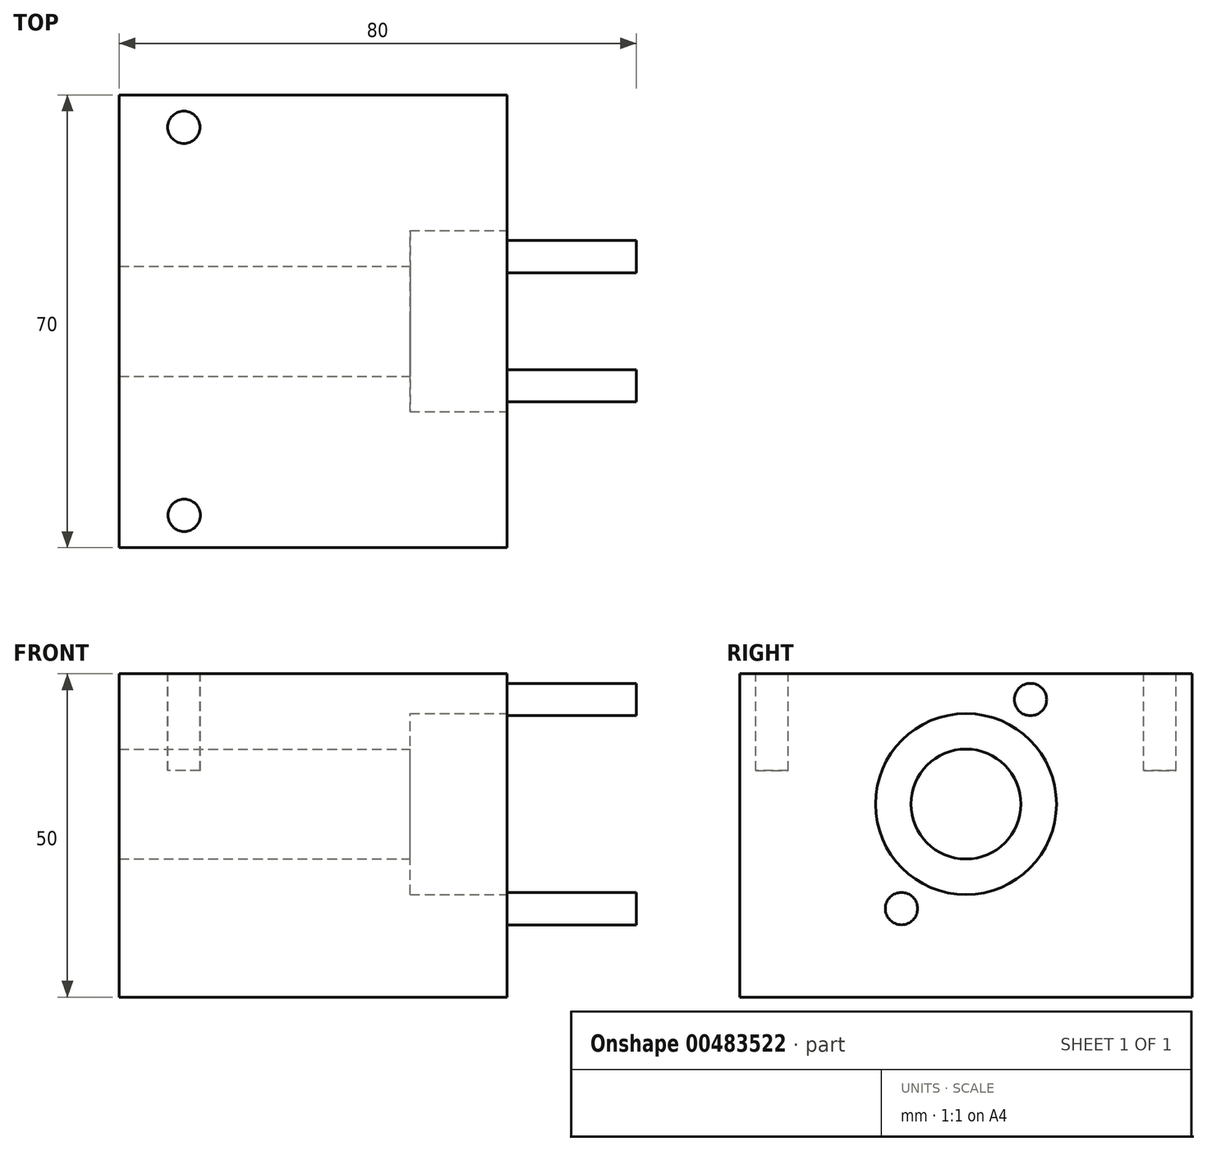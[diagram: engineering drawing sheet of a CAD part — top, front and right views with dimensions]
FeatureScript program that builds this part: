
annotation { "Feature Type Name" : "Feature", "Feature Type Description" : "" }
export const myFeature = defineFeature(function(context is Context, id is Id, definition is map)
    precondition{}
    {
        {
            var Q0;
            Q0=qCreatedBy(makeId("Top.planeOp"),FACE);
            var sketch = newSketch(context, id + "F0", { "sketchPlane" : qUnion([Q0])});
            skLineSegment(sketch, "E0.bottom", {"start": v(-38.54, 38.67) * mm, "end": v(41.46, 38.67) * mm});
            skLineSegment(sketch, "E0.top", {"start": v(-38.54, -31.33) * mm, "end": v(41.46, -31.33) * mm});
            skLineSegment(sketch, "E0.left", {"start": v(-38.54, 38.67) * mm, "end": v(-38.54, -31.33) * mm});
            skLineSegment(sketch, "E0.right", {"start": v(41.46, 38.67) * mm, "end": v(41.46, -31.33) * mm});
            skSolve(sketch);
        }
        {
            var Q0;
            Q0=makeQuery(id+"F0.imprint","IMPRINT",FACE,{"disambiguationData":[TD([[makeQuery(id+"F0.imprint","IMPRINT",EDGE,{"derivedFrom":sQuery(id+"F0.wireOp",EDGE,"E0.bottom")}),-1.0]])]});
            extrude(context, id + "F1", {"entities" : qUnion([Q0]), "depth" : 50 * mm});
        }
        {
            var Q0;
            Q0=makeQuery(id+"F1.opExtrude","CAP_FACE",FACE,{"disambiguationData":[OSD([sQuery(id+"F0.wireOp",EDGE,"E0.bottom"),sQuery(id+"F0.wireOp",EDGE,"E0.top"),sQuery(id+"F0.wireOp",EDGE,"E0.left"),sQuery(id+"F0.wireOp",EDGE,"E0.right")])],"isStart":false});
            var sketch = newSketch(context, id + "F2", { "sketchPlane" : qUnion([Q0])});
            skCircle(sketch, "E1", {"center": v(-28.54, 33.67) * mm, "radius": 2.5 * mm});
            skCircle(sketch, "E2.0.1.0", {"center": v(-28.48, -26.33) * mm, "radius": 2.5 * mm});
            skCircle(sketch, "E2.1.0.0", {"center": v(31.46, 33.52) * mm, "radius": 2.5 * mm});
            skCircle(sketch, "E2.1.1.0", {"center": v(31.52, -26.48) * mm, "radius": 2.5 * mm});
            skLineSegment(sketch, "E2.direction1", {"start": v(-28.54, 33.67) * mm, "end": v(31.46, 33.52) * mm, "construction": true});
            skLineSegment(sketch, "E2.direction2", {"start": v(-28.54, 33.67) * mm, "end": v(-28.48, -26.33) * mm, "construction": true});
            skSolve(sketch);
        }
        {
            var Q0;
            Q0 = qSketchRegion(id + "F2", true);
            extrude(context, id + "F3", {"entities" : qUnion([Q0]), "operationType" : NewBodyOperationType.REMOVE, "oppositeDirection" : true, "depth" : 15 * mm});
        }
        {
            var Q0;
            Q0=makeQuery(id+"F1.opExtrude","SWEPT_FACE",FACE,{"disambiguationData":[OSD([sQuery(id+"F0.wireOp",EDGE,"E0.right")])]});
            var sketch = newSketch(context, id + "F4", { "sketchPlane" : qUnion([Q0])});
            skPoint(sketch, "E3", {"position": v(3.67, 29.85) * mm});
            skPoint(sketch, "E3.positionSnap0", {"position": v(3.67, 50) * mm});
            skCircle(sketch, "E4", {"center": v(3.67, 29.85) * mm, "radius": 8.5 * mm});
            skCircle(sketch, "E5", {"center": v(3.67, 29.85) * mm, "radius": 14 * mm});
            skCircle(sketch, "E6", {"center": v(22.67, 29.85) * mm, "radius": 2.5 * mm});
            skCircle(sketch, "E7", {"center": v(-15.33, 29.85) * mm, "radius": 2.5 * mm});
            skCircle(sketch, "E8.1.1", {"center": v(-6.3, 46.02) * mm, "radius": 2.5 * mm});
            skLineSegment(sketch, "E8.anchor1", {"start": v(3.67, 29.85) * mm, "end": v(-15.33, 29.85) * mm, "construction": true});
            skLineSegment(sketch, "E8.anchor2", {"start": v(3.67, 29.85) * mm, "end": v(-6.3, 46.02) * mm, "construction": true});
            skCircle(sketch, "E9.MirrorC", {"center": v(-6.3, 13.68) * mm, "radius": 2.5 * mm});
            skCircle(sketch, "E10.1.0", {"center": v(13.65, 13.68) * mm, "radius": 2.5 * mm});
            skLineSegment(sketch, "E10.anchor1", {"start": v(3.67, 29.85) * mm, "end": v(22.67, 29.85) * mm, "construction": true});
            skLineSegment(sketch, "E10.anchor2", {"start": v(3.67, 29.85) * mm, "end": v(13.65, 13.68) * mm, "construction": true});
            skCircle(sketch, "E11.MirrorC", {"center": v(13.65, 46.02) * mm, "radius": 2.5 * mm});
            skSolve(sketch);
        }
        {
            var Q0;
            Q0=makeQuery(id+"F4.imprint","IMPRINT",FACE,{"disambiguationData":[TD([[makeQuery(id+"F4.imprint","IMPRINT",EDGE,{"derivedFrom":sQuery(id+"F4.wireOp",EDGE,"E4")}),1.0]])]});
            var Q1;
            Q1=sQuery(id+"F4.wireOp",EDGE,"E4");
            extrude(context, id + "F5", {"entities" : qUnion([Q0]), "operationType" : NewBodyOperationType.REMOVE, "surfaceEntities" : qUnion([Q1]), "oppositeDirection" : true, "depth" : 92.7 * mm});
        }
        {
            var Q0;
            Q0=makeQuery(id+"F4.imprint","IMPRINT",FACE,{"disambiguationData":[TD([[makeQuery(id+"F4.imprint","IMPRINT",EDGE,{"derivedFrom":sQuery(id+"F4.wireOp",EDGE,"E4")}),-1.0]])]});
            extrude(context, id + "F6", {"entities" : qUnion([Q0]), "operationType" : NewBodyOperationType.REMOVE, "oppositeDirection" : true, "depth" : 35 * mm});
        }
        {
            var Q0;
            Q0=makeQuery(id+"F4.imprint","IMPRINT",FACE,{"disambiguationData":[TD([[makeQuery(id+"F4.imprint","IMPRINT",EDGE,{"derivedFrom":sQuery(id+"F4.wireOp",EDGE,"E8.1.1")}),1.0]])]});
            var Q1;
            Q1=makeQuery(id+"F4.imprint","IMPRINT",FACE,{"disambiguationData":[TD([[makeQuery(id+"F4.imprint","IMPRINT",EDGE,{"derivedFrom":sQuery(id+"F4.wireOp",EDGE,"E7")}),1.0]])]});
            var Q2;
            Q2=makeQuery(id+"F4.imprint","IMPRINT",FACE,{"disambiguationData":[TD([[makeQuery(id+"F4.imprint","IMPRINT",EDGE,{"derivedFrom":sQuery(id+"F4.wireOp",EDGE,"E9.MirrorC")}),-1.0]])]});
            var Q3;
            Q3=makeQuery(id+"F4.imprint","IMPRINT",FACE,{"disambiguationData":[TD([[makeQuery(id+"F4.imprint","IMPRINT",EDGE,{"derivedFrom":sQuery(id+"F4.wireOp",EDGE,"E10.1.0")}),1.0]])]});
            var Q4;
            Q4=makeQuery(id+"F4.imprint","IMPRINT",FACE,{"disambiguationData":[TD([[makeQuery(id+"F4.imprint","IMPRINT",EDGE,{"derivedFrom":sQuery(id+"F4.wireOp",EDGE,"E6")}),1.0]])]});
            var Q5;
            Q5=makeQuery(id+"F4.imprint","IMPRINT",FACE,{"disambiguationData":[TD([[makeQuery(id+"F4.imprint","IMPRINT",EDGE,{"derivedFrom":sQuery(id+"F4.wireOp",EDGE,"E11.MirrorC")}),-1.0]])]});
            extrude(context, id + "F7", {"entities" : qUnion([Q0, Q1, Q2, Q3, Q4, Q5]), "operationType" : NewBodyOperationType.REMOVE, "oppositeDirection" : true, "depth" : 20 * mm});
        }
    });
